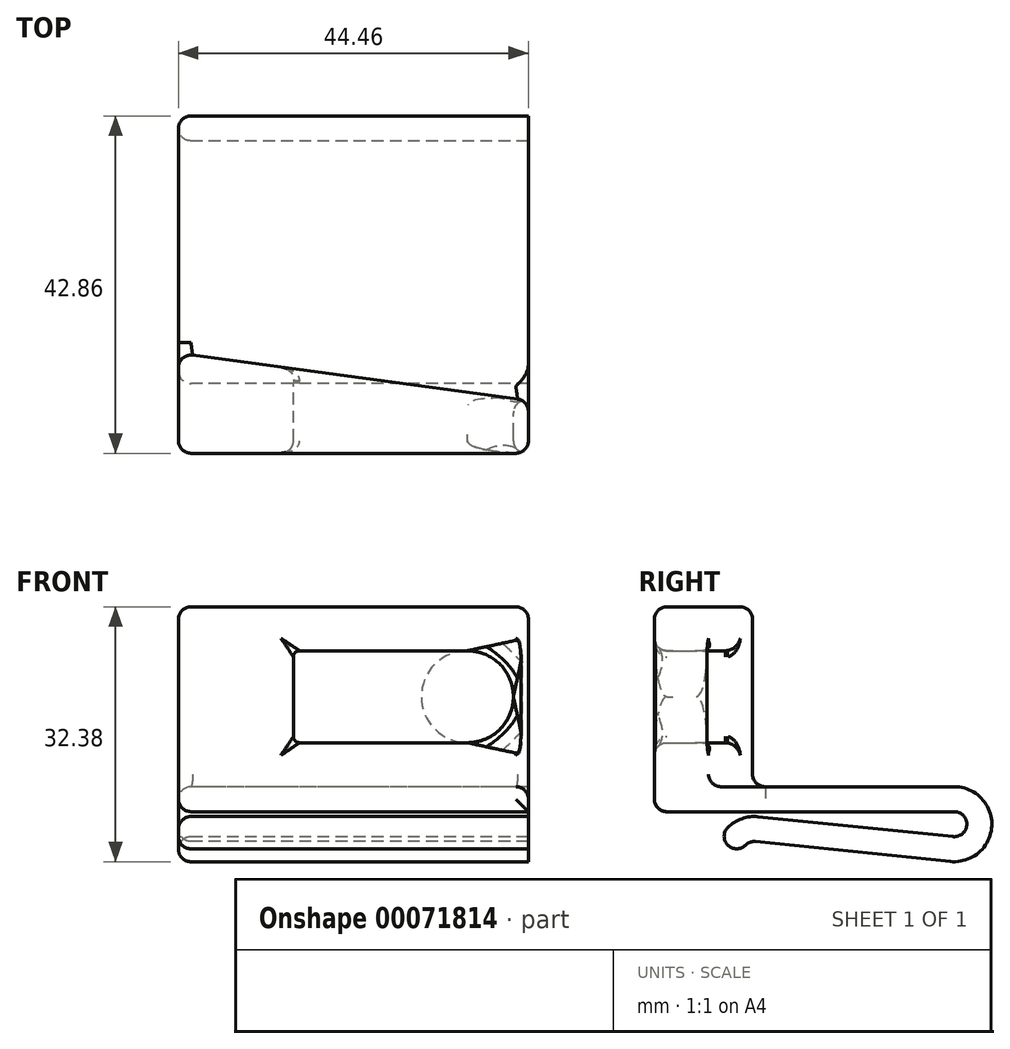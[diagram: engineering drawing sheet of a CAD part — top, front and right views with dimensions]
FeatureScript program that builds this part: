
annotation { "Feature Type Name" : "Feature", "Feature Type Description" : "" }
export const myFeature = defineFeature(function(context is Context, id is Id, definition is map)
    precondition{}
    {
        {
            var Q0;
            Q0=qCreatedBy(makeId("Front.planeOp"),FACE);
            var sketch = newSketch(context, id + "F0", { "sketchPlane" : qUnion([Q0])});
            skLineSegment(sketch, "E0.bottom", {"start": v(-22.22, -11.43) * mm, "end": v(22.23, -11.43) * mm});
            skLineSegment(sketch, "E0.top", {"start": v(-22.23, 11.43) * mm, "end": v(22.22, 11.43) * mm});
            skLineSegment(sketch, "E0.left", {"start": v(-22.22, -11.43) * mm, "end": v(-22.23, 11.43) * mm});
            skLineSegment(sketch, "E0.right", {"start": v(22.23, -11.43) * mm, "end": v(22.22, 11.43) * mm});
            skPoint(sketch, "E0.middle", {"position": v(0, 0) * mm});
            skSolve(sketch);
        }
        {
            var Q0;
            Q0=makeQuery(id+"F0.imprint","IMPRINT",FACE,{"disambiguationData":[TD([[makeQuery(id+"F0.imprint","IMPRINT",EDGE,{"derivedFrom":sQuery(id+"F0.wireOp",EDGE,"E0.bottom")}),1.0]])]});
            extrude(context, id + "F1", {"entities" : qUnion([Q0]), "depth" : 12.7 * mm});
        }
        {
            var Q0;
            Q0=makeQuery(id+"F1.opExtrude","CAP_FACE",FACE,{"disambiguationData":[OSD([sQuery(id+"F0.wireOp",EDGE,"E0.bottom"),sQuery(id+"F0.wireOp",EDGE,"E0.top"),sQuery(id+"F0.wireOp",EDGE,"E0.left"),sQuery(id+"F0.wireOp",EDGE,"E0.right")])],"isStart":true});
            var sketch = newSketch(context, id + "F2", { "sketchPlane" : qUnion([Q0])});
            skLineSegment(sketch, "E1.bottom", {"start": v(7.62, -5.84) * mm, "end": v(-20.32, -5.84) * mm});
            skLineSegment(sketch, "E1.top", {"start": v(7.62, 5.84) * mm, "end": v(-20.32, 5.84) * mm});
            skLineSegment(sketch, "E1.left", {"start": v(7.62, -5.84) * mm, "end": v(7.62, 5.84) * mm});
            skLineSegment(sketch, "E1.right", {"start": v(-20.32, -5.84) * mm, "end": v(-20.32, 5.84) * mm});
            skLineSegment(sketch, "E2", {"start": v(22.23, 0) * mm, "end": v(-22.23, 0) * mm, "construction": true});
            skSolve(sketch);
        }
        {
            var Q0;
            Q0=makeQuery(id+"F2.imprint","IMPRINT",FACE,{"disambiguationData":[TD([[makeQuery(id+"F2.imprint","IMPRINT",EDGE,{"derivedFrom":sQuery(id+"F2.wireOp",EDGE,"E1.bottom")}),-1.0]])]});
            extrude(context, id + "F3", {"entities" : qUnion([Q0]), "operationType" : NewBodyOperationType.REMOVE, "endBound" : BoundingType.UP_TO_NEXT, "oppositeDirection" : true, "depth" : 25.4 * mm});
        }
        {
            var Q0;
            Q0=makeQuery(id+"F1.opExtrude","SWEPT_FACE",FACE,{"disambiguationData":[OSD([sQuery(id+"F0.wireOp",EDGE,"E0.top")])]});
            var sketch = newSketch(context, id + "F4", { "sketchPlane" : qUnion([Q0])});
            skLineSegment(sketch, "E3", {"start": v(-22.23, 0) * mm, "end": v(22.23, -6) * mm});
            skSolve(sketch);
        }
        {
            var Q0;
            {var subQ0=sQuery(id+"F4.wireOp",EDGE,"gMgyRfRo-v2Ht-aM8K-1w6d-pH4m9GnYQ4Qn");Q0=makeQuery(id+"F4.imprint","IMPRINT",FACE,{"disambiguationData":[TD([[makeQuery(id+"F4.imprint","IMPRINT",EDGE,{"derivedFrom":subQ0}),-1.0]])]});}
            var Q1;
            {var subQ0=sQuery(id+"F4.wireOp",EDGE,"E3");Q1=makeQuery(id+"F4.imprint","IMPRINT",FACE,{"disambiguationData":[TD([[makeQuery(id+"F4.imprint","IMPRINT",EDGE,{"derivedFrom":subQ0}),1.0]])]});}
            var Q2;
            Q2=makeQuery(id+"F1.opExtrude","SWEPT_FACE",FACE,{"disambiguationData":[OSD([sQuery(id+"F0.wireOp",EDGE,"E0.bottom")])]});
            extrude(context, id + "F5", {"entities" : qUnion([Q0, Q1]), "operationType" : NewBodyOperationType.REMOVE, "endBound" : BoundingType.UP_TO_SURFACE, "oppositeDirection" : true, "endBoundEntityFace" : qUnion([Q2]), "depth" : 25.4 * mm});
        }
        {
            var Q0;
            Q0=makeQuery(id+"F1.opExtrude","SWEPT_FACE",FACE,{"disambiguationData":[OSD([sQuery(id+"F0.wireOp",EDGE,"E0.bottom")])]});
            var sketch = newSketch(context, id + "F6", { "sketchPlane" : qUnion([Q0])});
            skLineSegment(sketch, "E4.bottom", {"start": v(22.23, 12.7) * mm, "end": v(-22.23, 12.7) * mm});
            skLineSegment(sketch, "E4.top", {"start": v(22.23, -25.4) * mm, "end": v(-22.23, -25.4) * mm});
            skLineSegment(sketch, "E4.left", {"start": v(22.23, 12.7) * mm, "end": v(22.23, -25.4) * mm});
            skLineSegment(sketch, "E4.right", {"start": v(-22.23, 12.7) * mm, "end": v(-22.23, -25.4) * mm});
            skSolve(sketch);
        }
        {
            var Q0;
            {var subQ0=sQuery(id+"F6.wireOp",EDGE,"E4.top");Q0=makeQuery(id+"F6.imprint","IMPRINT",FACE,{"disambiguationData":[TD([[makeQuery(id+"F6.imprint","IMPRINT",EDGE,{"derivedFrom":subQ0}),-1.0]])]});}
            var Q1;
            {var subQ0=sQuery(id+"F6.wireOp",EDGE,"E4.bottom");Q1=makeQuery(id+"F6.imprint","IMPRINT",FACE,{"disambiguationData":[TD([[makeQuery(id+"F6.imprint","IMPRINT",EDGE,{"derivedFrom":subQ0}),-1.0]])]});}
            extrude(context, id + "F7", {"entities" : qUnion([Q0, Q1]), "operationType" : NewBodyOperationType.ADD, "depth" : 3.17 * mm});
        }
        {
            var Q0;
            Q0=makeQuery(id+"F7.boolean.opBoolean","MERGE",FACE,{"derivedFrom":[makeQuery(id+"F1.opExtrude","SWEPT_FACE",FACE,{"disambiguationData":[OSD([sQuery(id+"F0.wireOp",EDGE,"E0.left")])]}),makeQuery(id+"F7.opExtrude","SWEPT_FACE",FACE,{"disambiguationData":[OSD([sQuery(id+"F6.wireOp",EDGE,"E4.right")])]})]});
            var sketch = newSketch(context, id + "F8", { "sketchPlane" : qUnion([Q0])});
            skCircle(sketch, "E5", {"center": v(-25.4, -16.2) * mm, "radius": 1.59 * mm});
            skCircle(sketch, "E6", {"center": v(0, -19.98) * mm, "radius": 1.59 * mm});
            skCircle(sketch, "E7", {"center": v(-25.4, -16.2) * mm, "radius": 4.76 * mm});
            skCircle(sketch, "E8", {"center": v(0, -19.98) * mm, "radius": 4.76 * mm});
            skLineSegment(sketch, "E9", {"start": v(-24.92, -20.93) * mm, "end": v(-0.16, -18.4) * mm});
            skLineSegment(sketch, "E10", {"start": v(-25.24, -17.77) * mm, "end": v(-0.48, -15.24) * mm});
            skLineSegment(sketch, "E11", {"start": v(0, -19.98) * mm, "end": v(4.6, -18.75) * mm});
            skLineSegment(sketch, "E12", {"start": v(0, -19.98) * mm, "end": v(4.76, -19.98) * mm, "construction": true});
            skSolve(sketch);
        }
        {
            var Q0;
            {var subQ0=sQuery(id+"F8.wireOp",EDGE,"E9");var subQ1=sQuery(id+"F8.wireOp",EDGE,"E6");var subQ2=makeQuery(id+"F8.imprint","INTERSECT",VERTEX,{"derivedFrom":[subQ1,subQ0]});Q0=makeQuery(id+"F8.imprint","IMPRINT",FACE,{"disambiguationData":[TD([[makeQuery(id+"F8.imprint","IMPRINT",EDGE,{"disambiguationData":[TD([[subQ2,1.0]])],"derivedFrom":subQ1}),-1.0]])]});}
            var Q1;
            {var subQ0=sQuery(id+"F8.wireOp",EDGE,"E9");var subQ1=sQuery(id+"F8.wireOp",EDGE,"E7");var subQ2=makeQuery(id+"F8.imprint","INTERSECT",VERTEX,{"derivedFrom":[subQ1,subQ0]});Q1=makeQuery(id+"F8.imprint","IMPRINT",FACE,{"disambiguationData":[TD([[makeQuery(id+"F8.imprint","IMPRINT",EDGE,{"disambiguationData":[TD([[subQ2,-1.0]])],"derivedFrom":subQ1}),-1.0]])]});}
            var Q2;
            {var subQ6=sQuery(id+"F6.wireOp",EDGE,"E4.right");var subQ7=makeQuery(id+"F7.opExtrude","SWEPT_EDGE",EDGE,{"disambiguationData":[OSD([sQuery(id+"F6.wireOp",EDGE,"E4.top"),subQ6])]});Q2=makeQuery(id+"F8.imprint","IMPRINT",FACE,{"disambiguationData":[TD([[makeQuery(id+"F8.imprint","IMPRINT",EDGE,{"derivedFrom":subQ7}),1.0]])]});}
            var Q3;
            Q3=makeQuery(id+"F7.boolean.opBoolean","MERGE",FACE,{"derivedFrom":[makeQuery(id+"F1.opExtrude","SWEPT_FACE",FACE,{"disambiguationData":[OSD([sQuery(id+"F0.wireOp",EDGE,"E0.right")])]}),makeQuery(id+"F7.opExtrude","SWEPT_FACE",FACE,{"disambiguationData":[OSD([sQuery(id+"F6.wireOp",EDGE,"E4.left")])]})]});
            extrude(context, id + "F9", {"entities" : qUnion([Q0, Q1, Q2]), "operationType" : NewBodyOperationType.ADD, "endBound" : BoundingType.UP_TO_SURFACE, "oppositeDirection" : true, "endBoundEntityFace" : qUnion([Q3]), "depth" : 25.4 * mm});
        }
        {
            var Q0;
            Q0=makeQuery(id+"F9.opExtrude","SWEPT_EDGE",EDGE,{"disambiguationData":[OSD([sQuery(id+"F8.wireOp",EDGE,"E8"),sQuery(id+"F8.wireOp",EDGE,"E11")])]});
            var Q1;
            Q1=makeQuery(id+"F9.opExtrude","SWEPT_EDGE",EDGE,{"disambiguationData":[OSD([sQuery(id+"F8.wireOp",EDGE,"E6"),sQuery(id+"F8.wireOp",EDGE,"E11")])]});
            fillet(context, id + "F10", {"entities" : qUnion([Q0, Q1]), "radius" : 1.59 * mm, "tangentPropagation" : true, "allowEdgeOverflow" : false});
        }
        {
            var Q0;
            Q0=makeQuery(id+"F5.boolean.opBoolean","COPY",FACE,{"derivedFrom":makeQuery(id+"F5.opExtrude","SWEPT_FACE",FACE,{"disambiguationData":[OSD([sQuery(id+"F4.wireOp",EDGE,"gMgyRfRo-v2Ht-aM8K-1w6d-pH4m9GnYQ4Qn")])]})});
            var Q1;
            Q1=makeQuery(id+"F1.opExtrude","SWEPT_FACE",FACE,{"disambiguationData":[OSD([sQuery(id+"F0.wireOp",EDGE,"E0.top")])]});
            var Q2;
            {var subQ0=sQuery(id+"F6.wireOp",EDGE,"E4.right");Q2=makeQuery(id+"F9.boolean.opBoolean","MERGE",FACE,{"derivedFrom":[makeQuery(id+"F7.boolean.opBoolean","MERGE",FACE,{"derivedFrom":[makeQuery(id+"F1.opExtrude","SWEPT_FACE",FACE,{"disambiguationData":[OSD([sQuery(id+"F0.wireOp",EDGE,"E0.left")])]}),makeQuery(id+"F7.opExtrude","SWEPT_FACE",FACE,{"disambiguationData":[OSD([subQ0])]})]}),makeQuery(id+"F9.opExtrude","CAP_FACE",FACE,{"disambiguationData":[OSD([sQuery(id+"F6.wireOp",EDGE,"E4.top"),subQ0,sQuery(id+"F8.wireOp",EDGE,"E5"),sQuery(id+"F8.wireOp",EDGE,"E6"),sQuery(id+"F8.wireOp",EDGE,"E7"),sQuery(id+"F8.wireOp",EDGE,"E8"),sQuery(id+"F8.wireOp",EDGE,"E9"),sQuery(id+"F8.wireOp",EDGE,"E10"),sQuery(id+"F8.wireOp",EDGE,"E11")])],"isStart":true})]});}
            var Q3;
            Q3=makeQuery(id+"F7.boolean.opBoolean","MERGE",FACE,{"derivedFrom":[makeQuery(id+"F1.opExtrude","CAP_FACE",FACE,{"disambiguationData":[OSD([sQuery(id+"F0.wireOp",EDGE,"E0.bottom"),sQuery(id+"F0.wireOp",EDGE,"E0.top"),sQuery(id+"F0.wireOp",EDGE,"E0.left"),sQuery(id+"F0.wireOp",EDGE,"E0.right")])],"isStart":false}),makeQuery(id+"F7.opExtrude","SWEPT_FACE",FACE,{"disambiguationData":[OSD([sQuery(id+"F6.wireOp",EDGE,"E4.bottom")])]})]});
            var Q4;
            Q4=makeQuery(id+"F5.boolean.opBoolean","COPY",FACE,{"derivedFrom":makeQuery(id+"F5.opExtrude","SWEPT_FACE",FACE,{"disambiguationData":[OSD([sQuery(id+"F4.wireOp",EDGE,"E3")])]})});
            fillet(context, id + "F11", {"entities" : qUnion([Q0, Q1, Q2, Q3, Q4]), "radius" : 1.59 * mm, "tangentPropagation" : true, "allowEdgeOverflow" : false});
        }
        {
            var Q0;
            Q0=makeQuery(id+"F3.boolean.opBoolean","COPY",EDGE,{"derivedFrom":makeQuery(id+"F3.opExtrude","SWEPT_EDGE",EDGE,{"disambiguationData":[OSD([sQuery(id+"F2.wireOp",EDGE,"E1.bottom"),sQuery(id+"F2.wireOp",EDGE,"E1.left")])]})});
            var Q1;
            Q1=makeQuery(id+"F3.boolean.opBoolean","COPY",EDGE,{"derivedFrom":makeQuery(id+"F3.opExtrude","SWEPT_EDGE",EDGE,{"disambiguationData":[OSD([sQuery(id+"F2.wireOp",EDGE,"E1.top"),sQuery(id+"F2.wireOp",EDGE,"E1.left")])]})});
            fillet(context, id + "F12", {"entities" : qUnion([Q0, Q1]), "radius" : 0.8 * mm, "tangentPropagation" : true, "allowEdgeOverflow" : false});
        }
        {
            var Q0;
            Q0=makeQuery(id+"F3.boolean.opBoolean","COPY",EDGE,{"derivedFrom":makeQuery(id+"F3.opExtrude","SWEPT_EDGE",EDGE,{"disambiguationData":[OSD([sQuery(id+"F2.wireOp",EDGE,"E1.bottom"),sQuery(id+"F2.wireOp",EDGE,"E1.right")])]})});
            var Q1;
            Q1=makeQuery(id+"F3.boolean.opBoolean","COPY",EDGE,{"derivedFrom":makeQuery(id+"F3.opExtrude","SWEPT_EDGE",EDGE,{"disambiguationData":[OSD([sQuery(id+"F2.wireOp",EDGE,"E1.top"),sQuery(id+"F2.wireOp",EDGE,"E1.right")])]})});
            fillet(context, id + "F13", {"entities" : qUnion([Q0, Q1]), "radius" : 5.84 * mm, "tangentPropagation" : true, "allowEdgeOverflow" : false});
        }
    });
